# Revit family: Gira_067667
name_source: partatom
category: Electrical Fixtures
revit_build: Autodesk Revit 2017 (Build: 20160225_1515(x64)
units: mm (PartAtom-declared; Revit-internal decimal feet)

## family parameters
Cut with Voids When Loaded = No
Host = Face
Maintain Annotation Orientation = No
Part Type = Normal
Room Calculation Point = No
Round Connector Dimension = Use Diameter
Shared = No

## types (1)
- Rocker in.sp. Gira TX_44 (WP FM) anthra.
    Available = No
    BIM (1) = https://media.stage.bim.site und Tasten.rfa?public/gira/36a6b08/TX44_Abdeckung_Schalten und Tasten.rfa
    Category = Control element/cover plate for domestic switching devices
    Data sheet (1) = https://katalog.gira.de
    Default Elevation = 1219 mm
    Description = Rock.in.sp. TX_44 AN,Rocker with inscription space,,anthracite,Notes :,- Theft-prevention implemented via optional screw-in clamp piece. This makes plugging of cover frame unnecessary.
    GTIN = 4010337676676
    HAN = 067667
    HeinzeBIM = https://bimportal.heinze.de
    Manufacturer = Gira
    Manufacturer URL = https://www.gira.de
    Model = Single rocker
    Monitoring window/light outlet = No
    Name = Rocker in.sp. Gira TX_44 (WP FM) anthra.
    Scannable symbol / barrier free = No
    Suitable for touch sensor connector for bus system = No
    URL = http://katalog.gira.de
    With exchangeable lens/symbol = No

## geometry (parser evidence)
native form markers: Blend x2, Sweep x3
no freeform markers — native parametric forms only
